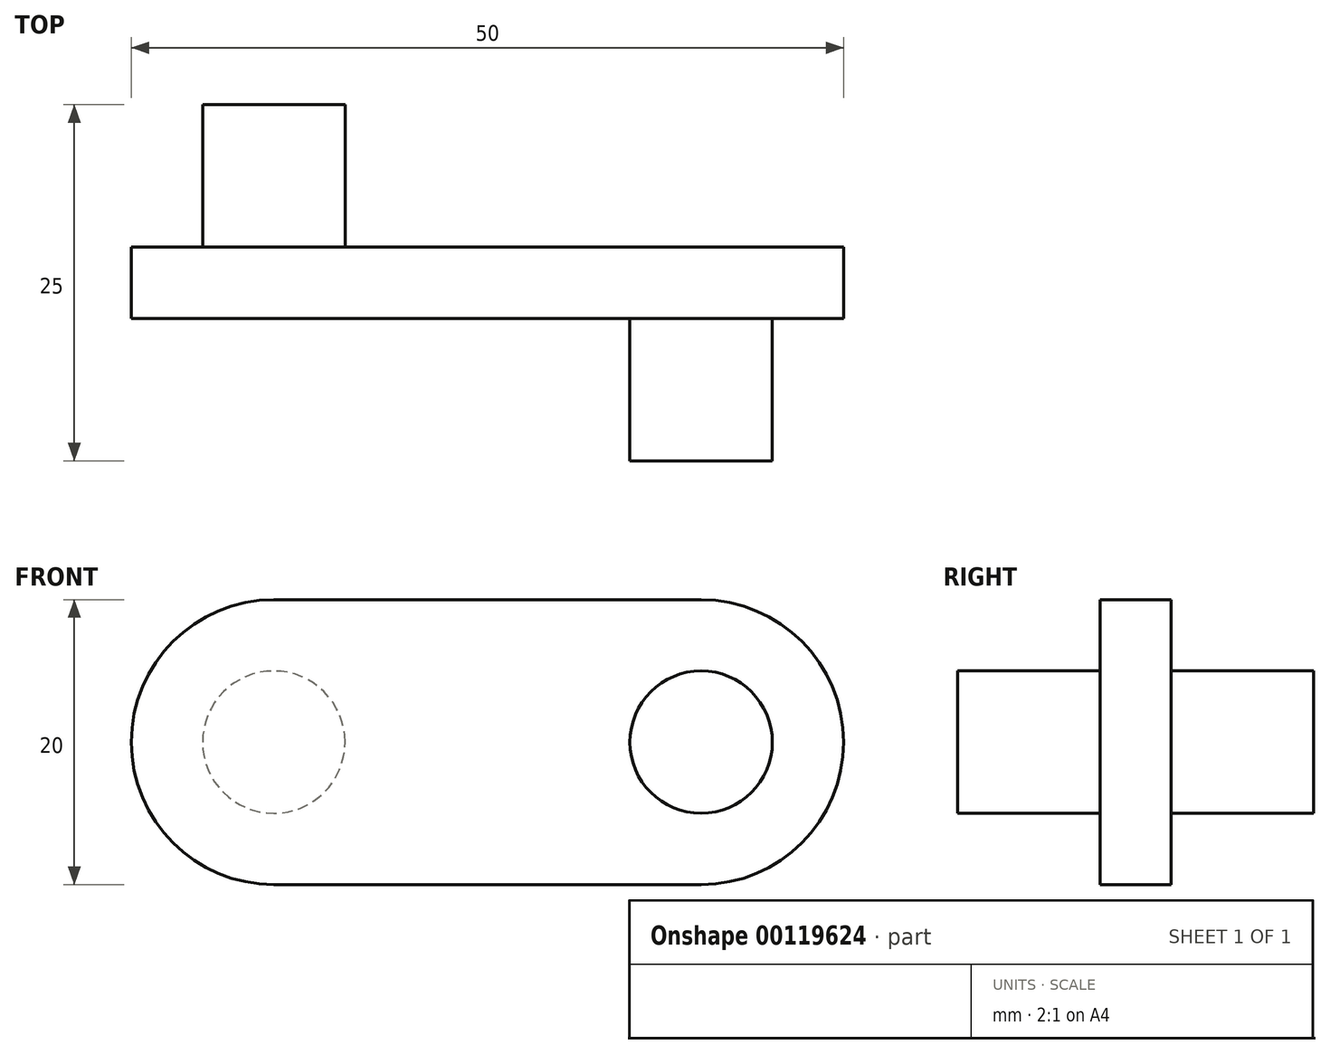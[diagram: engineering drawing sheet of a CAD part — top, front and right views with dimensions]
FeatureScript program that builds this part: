
annotation { "Feature Type Name" : "Feature", "Feature Type Description" : "" }
export const myFeature = defineFeature(function(context is Context, id is Id, definition is map)
    precondition{}
    {
        {
            var Q0;
            Q0=qCreatedBy(makeId("Front.planeOp"),FACE);
            var sketch = newSketch(context, id + "F0", { "sketchPlane" : qUnion([Q0])});
            skLineSegment(sketch, "E0", {"start": v(0, 0) * mm, "end": v(30, 0) * mm});
            skLineSegment(sketch, "E1", {"start": v(0, 20) * mm, "end": v(30, 20) * mm});
            skArc(sketch, "E2", {"start": v(0, 20) * mm, "mid": v(-10, 10) * mm, "end": v(0, 0) * mm});
            skArc(sketch, "E3", {"start": v(30, 0) * mm, "mid": v(40, 10) * mm, "end": v(30, 20) * mm});
            skSolve(sketch);
        }
        {
            var Q0;
            Q0 = qSketchRegion(id + "F0", true);
            extrude(context, id + "F1", {"entities" : qUnion([Q0]), "depth" : 5 * mm});
        }
        {
            var Q0;
            Q0=makeQuery(id+"F1.opExtrude","CAP_FACE",FACE,{"disambiguationData":[OSD([sQuery(id+"F0.wireOp",EDGE,"E0"),sQuery(id+"F0.wireOp",EDGE,"E1"),sQuery(id+"F0.wireOp",EDGE,"E2"),sQuery(id+"F0.wireOp",EDGE,"E3")])],"isStart":false});
            var sketch = newSketch(context, id + "F2", { "sketchPlane" : qUnion([Q0])});
            skCircle(sketch, "E4", {"center": v(30, 10) * mm, "radius": 5 * mm});
            skSolve(sketch);
        }
        {
            var Q0;
            Q0=makeQuery(id+"F2.imprint","IMPRINT",FACE,{"disambiguationData":[TD([[makeQuery(id+"F2.imprint","IMPRINT",EDGE,{"derivedFrom":sQuery(id+"F2.wireOp",EDGE,"E4")}),1.0]])]});
            extrude(context, id + "F3", {"entities" : qUnion([Q0]), "operationType" : NewBodyOperationType.ADD, "depth" : 10 * mm});
        }
        {
            var Q0;
            Q0=makeQuery(id+"F0.imprint","IMPRINT",FACE,{"disambiguationData":[TD([[makeQuery(id+"F0.imprint","IMPRINT",EDGE,{"derivedFrom":sQuery(id+"F0.wireOp",EDGE,"E0")}),1.0]])]});
            var sketch = newSketch(context, id + "F4", { "sketchPlane" : qUnion([Q0])});
            skCircle(sketch, "E5", {"center": v(0, 10) * mm, "radius": 5 * mm});
            skSolve(sketch);
        }
        {
            var Q0;
            Q0 = qSketchRegion(id + "F4", true);
            extrude(context, id + "F5", {"entities" : qUnion([Q0]), "operationType" : NewBodyOperationType.ADD, "oppositeDirection" : true, "depth" : 10 * mm});
        }
    });
